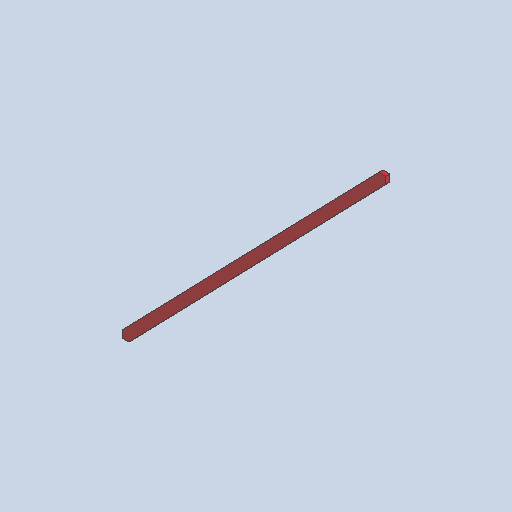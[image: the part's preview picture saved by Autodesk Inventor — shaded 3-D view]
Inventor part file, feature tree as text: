
AUTODESK INVENTOR PART (.ipt)
format: ipt  version: 2025.1 (Build 291241020, 241B)  size: 262,144 bytes
history: native  units: in
note: dims shown in document units (in); Inventor stores cm internally (conversion verified against a paired STEP export)
features: other x7, reference x4, plane x1, extrude x1, sketch x1
ambient origin geometry x8: Origin, YZ Plane, XZ Plane, XY Plane, X Axis, Y Axis, Z Axis, Center Point
bodies: Solid1 (feature_tree)
feature tree (14):
  plane  "Work Plane1"
  extrude  "Extrusion1"  [1 undecoded]
  sketch  "Sketch1"  dims[d2=1.5in d3=0.0in]
  reference  "Reference1"
  reference  "Reference2"
  reference  "Reference3"
  reference  "Reference4"
  other  "<userpath>\Documents\Tburn24\layer2\layer2.iam"
  other  "layer2.iam"
  other  "8'x2x4:4"
  other  "8'x2x4:5"
  other  "12'x2x4:2"
  other  "8'x2x4:1"
  other  "Finish1"
note: 1 required parameter value undecoded (feature->parameter linkage not recoverable at this tier; creation-order binding heuristic only, values carry confidence <= 0.55)
